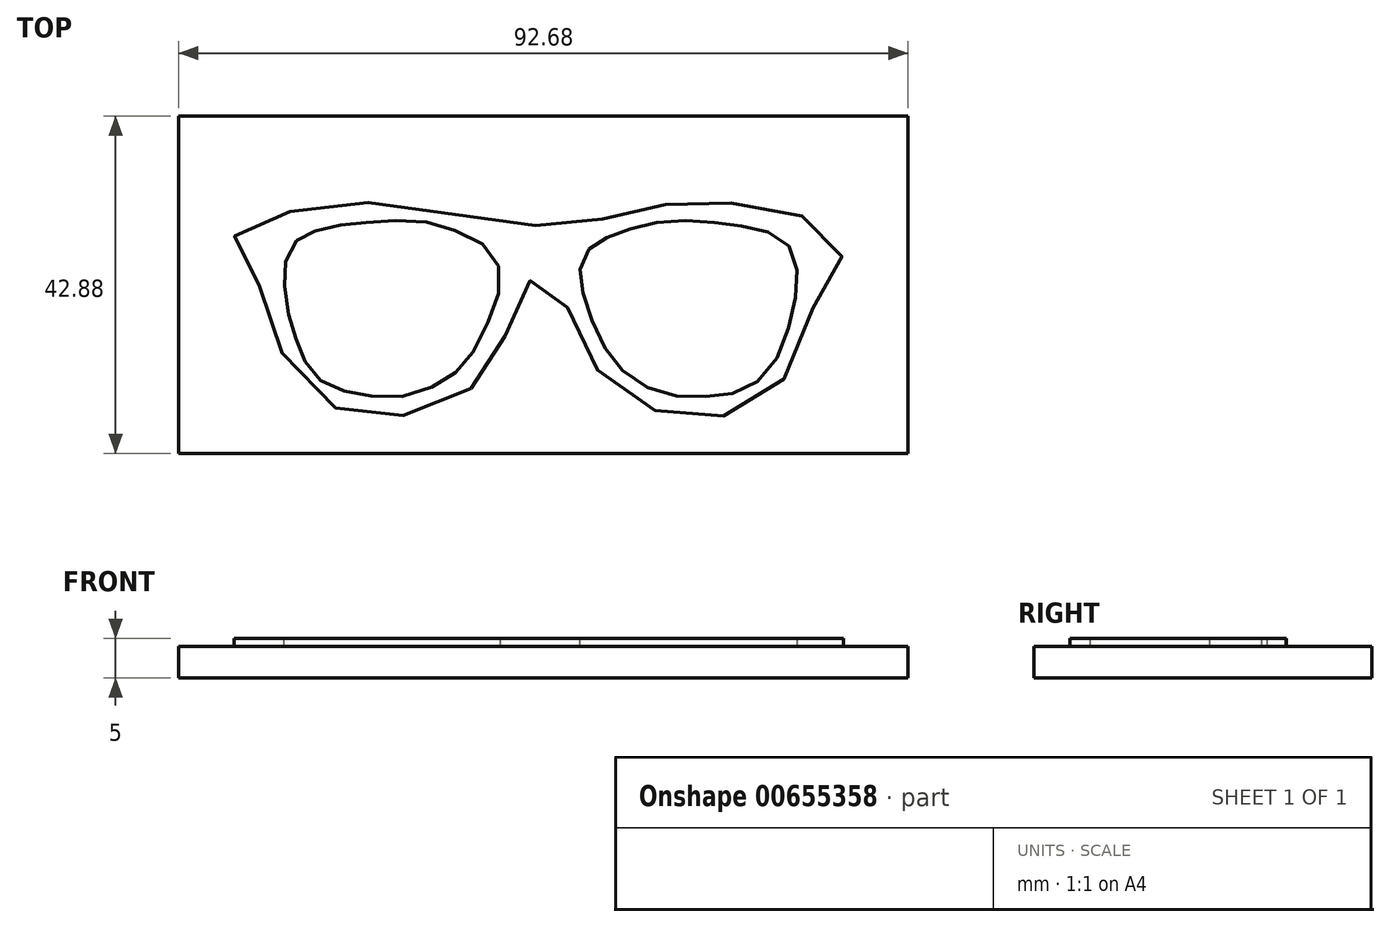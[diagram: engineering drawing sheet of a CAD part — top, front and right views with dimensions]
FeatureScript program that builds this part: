
annotation { "Feature Type Name" : "Feature", "Feature Type Description" : "" }
export const myFeature = defineFeature(function(context is Context, id is Id, definition is map)
    precondition{}
    {
        {
            var Q0;
            Q0=qCreatedBy(makeId("Top.planeOp"),FACE);
            var sketch = newSketch(context, id + "F0", { "sketchPlane" : qUnion([Q0])});
            skFitSpline(sketch, "E0", {"points": [v(-66.6, 23.53) * mm, v(-68.75, 22.45) * mm, v(-70.3, 19.83) * mm, v(-70.42, 16.37) * mm, v(-69.7, 11.84) * mm, v(-68.52, 8.62) * mm, v(-67.08, 5.64) * mm, v(-64.1, 3.6) * mm, v(-60.17, 2.65) * mm, v(-54.89, 2.62) * mm, v(-50.03, 4.68) * mm, v(-47.17, 7.19) * mm, v(-44.38, 12.49) * mm, v(-43.05, 17.1) * mm, v(-44.3, 21.02) * mm, v(-48.72, 23.53) * mm, v(-53.45, 24.8) * mm, v(-58.93, 24.71) * mm, v(-62.8, 24.36) * mm, v(-66.6, 23.53) * mm]});
            skFitSpline(sketch, "E1", {"points": [v(-38.58, 24.24) * mm, v(-33.97, 24.46) * mm, v(-28.8, 25.31) * mm, v(-24.63, 26.27) * mm, v(-20.15, 27.2) * mm, v(-15.92, 27.2) * mm, v(-9.95, 26.67) * mm, v(-4.83, 25.43) * mm, v(0, 23.6) * mm, v(0, 19.66) * mm, v(-2.1, 17.7) * mm, v(-3.63, 12.22) * mm, v(-5.92, 6.06) * mm, v(-10.11, 2.34) * mm, v(-14.91, 0) * mm, v(-19.5, 0) * mm, v(-25.22, 1.34) * mm, v(-29.63, 4.56) * mm, v(-32.62, 8.86) * mm, v(-34.52, 13.75) * mm, v(-36.04, 16.95) * mm, v(-38.82, 17.44) * mm, v(-40.37, 15.9) * mm, v(-41.92, 11.36) * mm, v(-44.54, 6.59) * mm, v(-46.45, 3.85) * mm, v(-50.98, 0.98) * mm, v(-56.7, 0) * mm, v(-60.17, 0) * mm, v(-68.04, 3.3) * mm, v(-70.83, 8.1) * mm, v(-72.93, 13.5) * mm, v(-74.12, 17.44) * mm, v(-76.53, 19.95) * mm, v(-76.53, 23.88) * mm, v(-75.04, 24.97) * mm, v(-67.03, 26.48) * mm, v(-61.36, 27.2) * mm, v(-52.77, 26.27) * mm, v(-45.62, 25.08) * mm, v(-38.58, 24.24) * mm]});
            skFitSpline(sketch, "E2", {"points": [v(-31.78, 21.25) * mm, v(-29.33, 22.77) * mm, v(-25.7, 24.04) * mm, v(-20.65, 24.88) * mm, v(-15.42, 24.54) * mm, v(-10.78, 23.87) * mm, v(-6.9, 22.18) * mm, v(-5.38, 18.56) * mm, v(-5.89, 13.58) * mm, v(-7.91, 7.42) * mm, v(-11.8, 3.54) * mm, v(-16.35, 2.53) * mm, v(-21.5, 2.7) * mm, v(-26.8, 5.15) * mm, v(-30.1, 9.2) * mm, v(-32.2, 14.5) * mm, v(-32.96, 18.3) * mm, v(-31.78, 21.25) * mm]});
            skSolve(sketch);
        }
        {
            var Q0;
            Q0 = qSketchRegion(id + "F0", true);
            extrude(context, id + "F1", {"entities" : qUnion([Q0]), "depth" : 5 * mm, "offsetDistance" : 25 * mm});
        }
        {
            var Q0;
            Q0=qCreatedBy(makeId("Top.planeOp"),FACE);
            var sketch = newSketch(context, id + "F2", { "sketchPlane" : qUnion([Q0])});
            skLineSegment(sketch, "E3.bottom", {"start": v(-83.94, 38.14) * mm, "end": v(8.74, 38.14) * mm});
            skLineSegment(sketch, "E3.top", {"start": v(-83.94, -4.74) * mm, "end": v(8.74, -4.74) * mm});
            skLineSegment(sketch, "E3.left", {"start": v(-83.94, 38.14) * mm, "end": v(-83.94, -4.74) * mm});
            skLineSegment(sketch, "E3.right", {"start": v(8.74, 38.14) * mm, "end": v(8.74, -4.74) * mm});
            skSolve(sketch);
        }
        {
            var Q0;
            Q0 = qSketchRegion(id + "F2", true);
            extrude(context, id + "F3", {"entities" : qUnion([Q0]), "operationType" : NewBodyOperationType.ADD, "depth" : 4 * mm, "offsetDistance" : 25 * mm});
        }
    });
